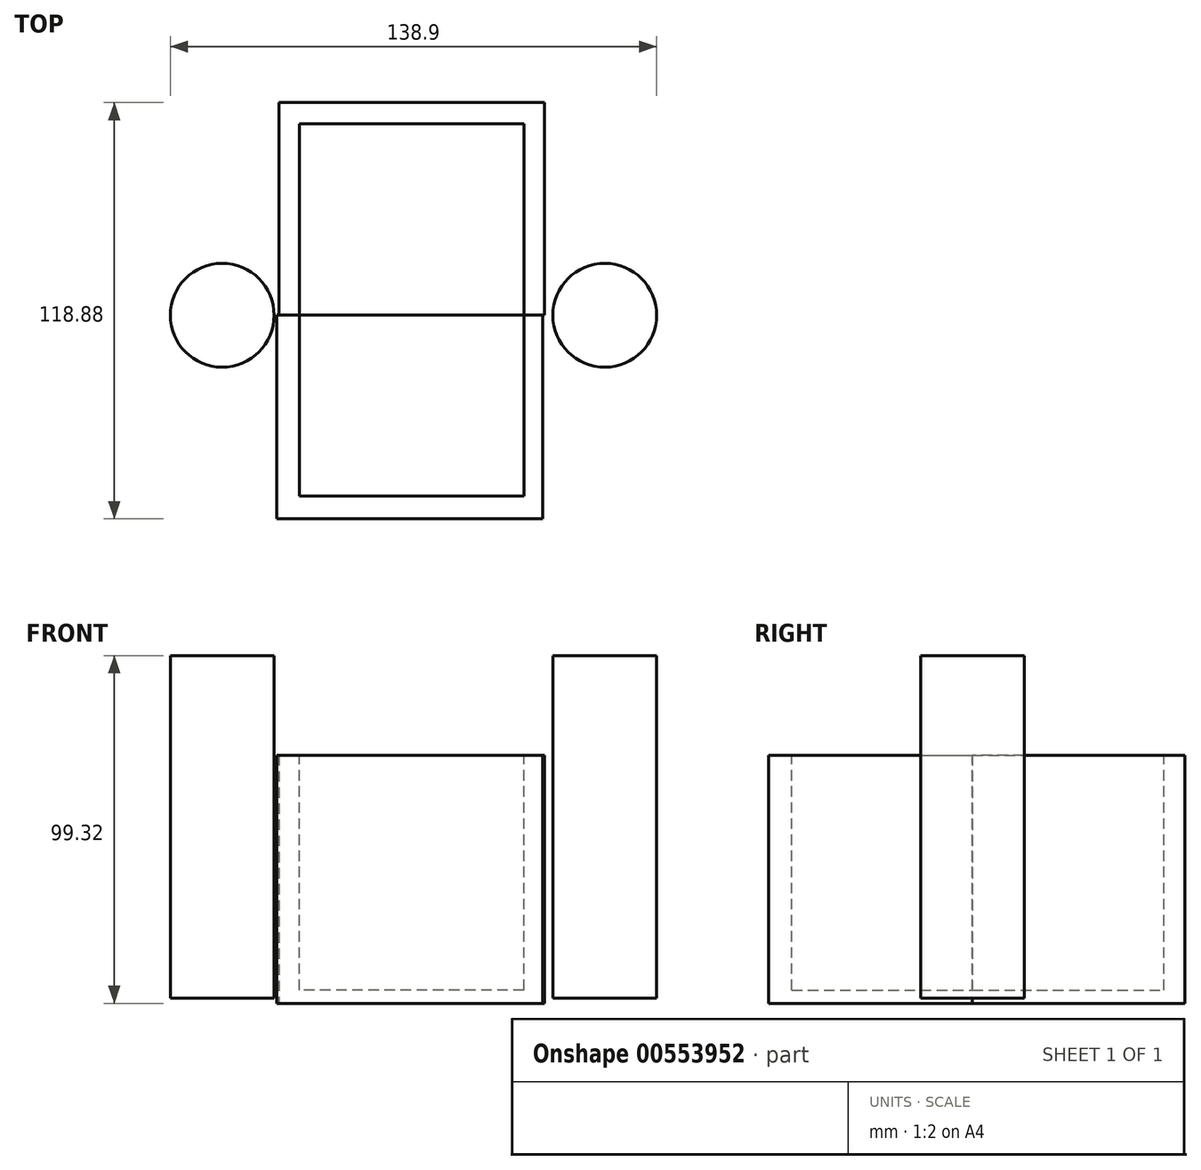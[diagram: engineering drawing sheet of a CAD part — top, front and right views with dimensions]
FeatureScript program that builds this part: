
annotation { "Feature Type Name" : "Feature", "Feature Type Description" : "" }
export const myFeature = defineFeature(function(context is Context, id is Id, definition is map)
    precondition{}
    {
        {
            var Q0;
            Q0=qCreatedBy(makeId("Front.planeOp"),FACE);
            var sketch = newSketch(context, id + "F0", { "sketchPlane" : qUnion([Q0])});
            skLineSegment(sketch, "E0.bottom", {"start": v(-39.01, 0) * mm, "end": v(36.88, 0) * mm});
            skLineSegment(sketch, "E0.top", {"start": v(-39.01, -70.87) * mm, "end": v(36.88, -70.87) * mm});
            skLineSegment(sketch, "E0.left", {"start": v(-39.01, 0) * mm, "end": v(-39.01, -70.87) * mm});
            skLineSegment(sketch, "E0.right", {"start": v(36.88, 0) * mm, "end": v(36.88, -70.87) * mm});
            skSolve(sketch);
        }
        {
            var Q0;
            Q0=qCreatedBy(makeId("Top.planeOp"),FACE);
            var sketch = newSketch(context, id + "F1", { "sketchPlane" : qUnion([Q0])});
            skCircle(sketch, "E1", {"center": v(-54.63, 0) * mm, "radius": 14.82 * mm});
            skCircle(sketch, "E2.MirrorC", {"center": v(54.63, 0) * mm, "radius": 14.82 * mm});
            skSolve(sketch);
        }
        {
            var Q0;
            Q0 = qSketchRegion(id + "F1", true);
            extrude(context, id + "F2", {"entities" : qUnion([Q0]), "oppositeDirection" : true, "depth" : 69.34 * mm, "offsetDistance" : 25.4 * mm});
        }
        {
            var Q0;
            Q0=makeQuery(id+"F0.imprint","IMPRINT",FACE,{"disambiguationData":[TD([[makeQuery(id+"F0.imprint","IMPRINT",EDGE,{"derivedFrom":sQuery(id+"F0.wireOp",EDGE,"E0.bottom")}),-1.0]])]});
            extrude(context, id + "F3", {"entities" : qUnion([Q0]), "operationType" : NewBodyOperationType.ADD, "depth" : 58.17 * mm, "offsetDistance" : 25.4 * mm});
        }
        {
            var Q0;
            Q0=qCreatedBy(makeId("Front.planeOp"),FACE);
            var sketch = newSketch(context, id + "F4", { "sketchPlane" : qUnion([Q0])});
            skLineSegment(sketch, "E3.bottom", {"start": v(37.43, 0) * mm, "end": v(-38.47, 0) * mm});
            skLineSegment(sketch, "E3.top", {"start": v(37.43, -70.87) * mm, "end": v(-38.47, -70.87) * mm});
            skLineSegment(sketch, "E3.left", {"start": v(37.43, 0) * mm, "end": v(37.43, -70.87) * mm});
            skLineSegment(sketch, "E3.right", {"start": v(-38.47, 0) * mm, "end": v(-38.47, -70.87) * mm});
            skSolve(sketch);
        }
        {
            var Q0;
            Q0=makeQuery(id+"F4.imprint","IMPRINT",FACE,{"disambiguationData":[TD([[makeQuery(id+"F4.imprint","IMPRINT",EDGE,{"derivedFrom":sQuery(id+"F4.wireOp",EDGE,"E3.bottom")}),1.0]])]});
            extrude(context, id + "F5", {"entities" : qUnion([Q0]), "oppositeDirection" : true, "depth" : 60.7 * mm, "offsetDistance" : 25.4 * mm});
        }
        {
            var Q0;
            Q0=qCreatedBy(makeId("Top.planeOp"),FACE);
            var sketch = newSketch(context, id + "F6", { "sketchPlane" : qUnion([Q0])});
            skLineSegment(sketch, "E4.bottom", {"start": v(-32.57, -51.58) * mm, "end": v(31.53, -51.58) * mm});
            skLineSegment(sketch, "E4.top", {"start": v(-32.57, 54.7) * mm, "end": v(31.53, 54.7) * mm});
            skLineSegment(sketch, "E4.left", {"start": v(-32.57, -51.58) * mm, "end": v(-32.57, 54.7) * mm});
            skLineSegment(sketch, "E4.right", {"start": v(31.53, -51.58) * mm, "end": v(31.53, 54.7) * mm});
            skSolve(sketch);
        }
        {
            var Q0;
            Q0 = qSketchRegion(id + "F6", true);
            extrude(context, id + "F7", {"entities" : qUnion([Q0]), "operationType" : NewBodyOperationType.REMOVE, "oppositeDirection" : true, "depth" : 67.06 * mm, "offsetDistance" : 25.4 * mm});
        }
        {
            var Q0;
            Q0 = qSketchRegion(id + "F1", true);
            extrude(context, id + "F8", {"entities" : qUnion([Q0]), "operationType" : NewBodyOperationType.ADD, "depth" : 28.45 * mm, "offsetDistance" : 25.4 * mm});
        }
    });
